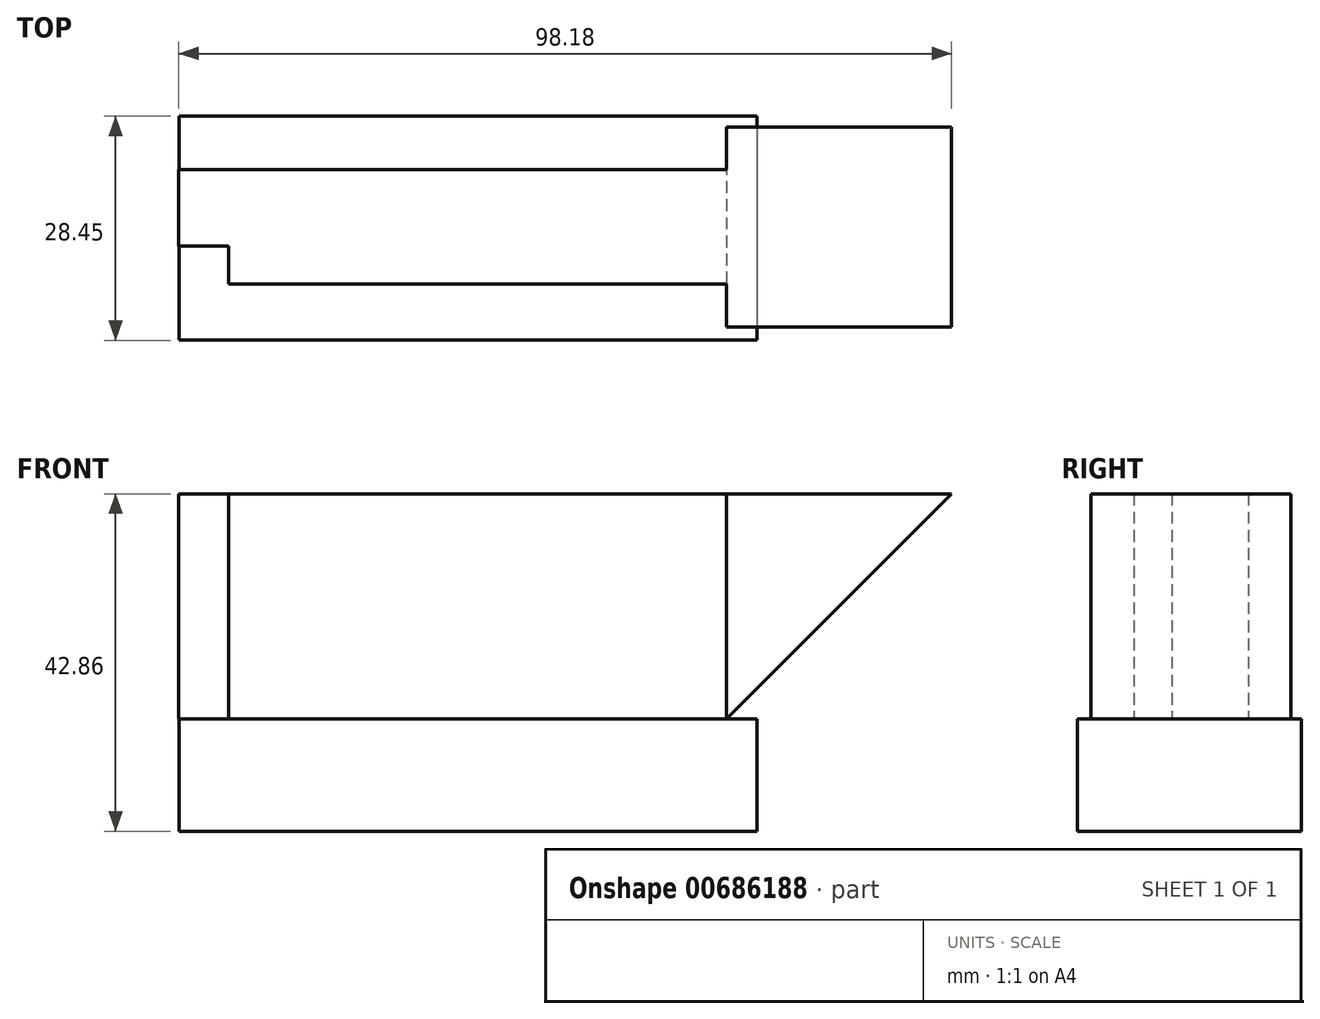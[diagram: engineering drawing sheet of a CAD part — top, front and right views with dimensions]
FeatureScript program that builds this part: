
annotation { "Feature Type Name" : "Feature", "Feature Type Description" : "" }
export const myFeature = defineFeature(function(context is Context, id is Id, definition is map)
    precondition{}
    {
        {
            var Q0;
            Q0=qCreatedBy(makeId("Top.planeOp"),FACE);
            var sketch = newSketch(context, id + "F0", { "sketchPlane" : qUnion([Q0])});
            skLineSegment(sketch, "E0.bottom", {"start": v(28.58, -14.39) * mm, "end": v(0, -14.39) * mm});
            skLineSegment(sketch, "E0.top", {"start": v(28.58, 11.01) * mm, "end": v(0, 11.01) * mm});
            skLineSegment(sketch, "E0.left", {"start": v(28.58, -14.39) * mm, "end": v(28.58, 11.01) * mm});
            skLineSegment(sketch, "E0.right", {"start": v(0, -14.39) * mm, "end": v(0, -8.96) * mm});
            skLineSegment(sketch, "E1.bottom", {"start": v(0, 5.58) * mm, "end": v(-69.6, 5.58) * mm});
            skLineSegment(sketch, "E1.top", {"start": v(0, -8.96) * mm, "end": v(-63.25, -8.96) * mm});
            skLineSegment(sketch, "E1.right", {"start": v(-69.6, 5.58) * mm, "end": v(-69.6, -4.13) * mm});
            skLineSegment(sketch, "E2.trimOffspring", {"start": v(0, 5.58) * mm, "end": v(0, 11.01) * mm});
            skLineSegment(sketch, "E3.top", {"start": v(-69.6, -4.13) * mm, "end": v(-63.25, -4.13) * mm});
            skLineSegment(sketch, "E3.right", {"start": v(-63.25, -8.96) * mm, "end": v(-63.25, -4.13) * mm});
            skPoint(sketch, "E4.orphan", {"position": v(-69.6, -8.96) * mm});
            skLineSegment(sketch, "E5.left", {"start": v(-69.6, -4.13) * mm, "end": v(-69.6, 5.58) * mm});
            skPoint(sketch, "E5.bottom.start.orphan", {"position": v(-69.6, -15.91) * mm});
            skSolve(sketch);
        }
        {
            var Q0;
            {var subQ0=sQuery(id+"F0.wireOp",EDGE,"E0.left");Q0=makeQuery(id+"F0.imprint","IMPRINT",FACE,{"disambiguationData":[TD([[makeQuery(id+"F0.imprint","IMPRINT",EDGE,{"derivedFrom":subQ0}),1.0]])]});}
            var Q1;
            {var subQ0=sQuery(id+"F0.wireOp",EDGE,"E0.right");Q1=makeQuery(id+"F0.imprint","IMPRINT",FACE,{"disambiguationData":[TD([[makeQuery(id+"F0.imprint","IMPRINT",EDGE,{"derivedFrom":subQ0}),-1.0]])]});}
            extrude(context, id + "F1", {"entities" : qUnion([Q0, Q1]), "depth" : 28.57 * mm, "offsetDistance" : 25.4 * mm});
        }
        {
            var Q0;
            Q0=qCreatedBy(makeId("Top.planeOp"),FACE);
            var sketch = newSketch(context, id + "F2", { "sketchPlane" : qUnion([Q0])});
            skLineSegment(sketch, "E6.bottom", {"start": v(3.84, 12.35) * mm, "end": v(-69.57, 12.35) * mm});
            skLineSegment(sketch, "E6.top", {"start": v(3.84, -16.1) * mm, "end": v(-69.57, -16.1) * mm});
            skLineSegment(sketch, "E6.left", {"start": v(3.84, 12.35) * mm, "end": v(3.84, -16.1) * mm});
            skLineSegment(sketch, "E6.right", {"start": v(-69.57, 12.35) * mm, "end": v(-69.57, -16.1) * mm});
            skSolve(sketch);
        }
        {
            var Q0;
            Q0 = qSketchRegion(id + "F2", true);
            extrude(context, id + "F3", {"entities" : qUnion([Q0]), "operationType" : NewBodyOperationType.ADD, "oppositeDirection" : true, "depth" : 14.29 * mm, "offsetDistance" : 25.4 * mm});
        }
        {
            var Q0;
            Q0=makeQuery(id+"F1.opExtrude","SWEPT_FACE",FACE,{"disambiguationData":[OSD([sQuery(id+"F0.wireOp",EDGE,"E0.bottom")])]});
            var sketch = newSketch(context, id + "F4", { "sketchPlane" : qUnion([Q0])});
            skLineSegment(sketch, "E7", {"start": v(28.58, 28.58) * mm, "end": v(0, 0) * mm});
            skSolve(sketch);
        }
        {
            var Q0;
            {var subQ0=sQuery(id+"F4.wireOp",EDGE,"E7");Q0=makeQuery(id+"F4.imprint","IMPRINT",FACE,{"disambiguationData":[TD([[makeQuery(id+"F4.imprint","IMPRINT",EDGE,{"derivedFrom":subQ0}),1.0]])]});}
            extrude(context, id + "F5", {"entities" : qUnion([Q0]), "operationType" : NewBodyOperationType.REMOVE, "endBound" : BoundingType.THROUGH_ALL, "oppositeDirection" : true, "depth" : 25.4 * mm, "offsetDistance" : 25.4 * mm});
        }
    });
